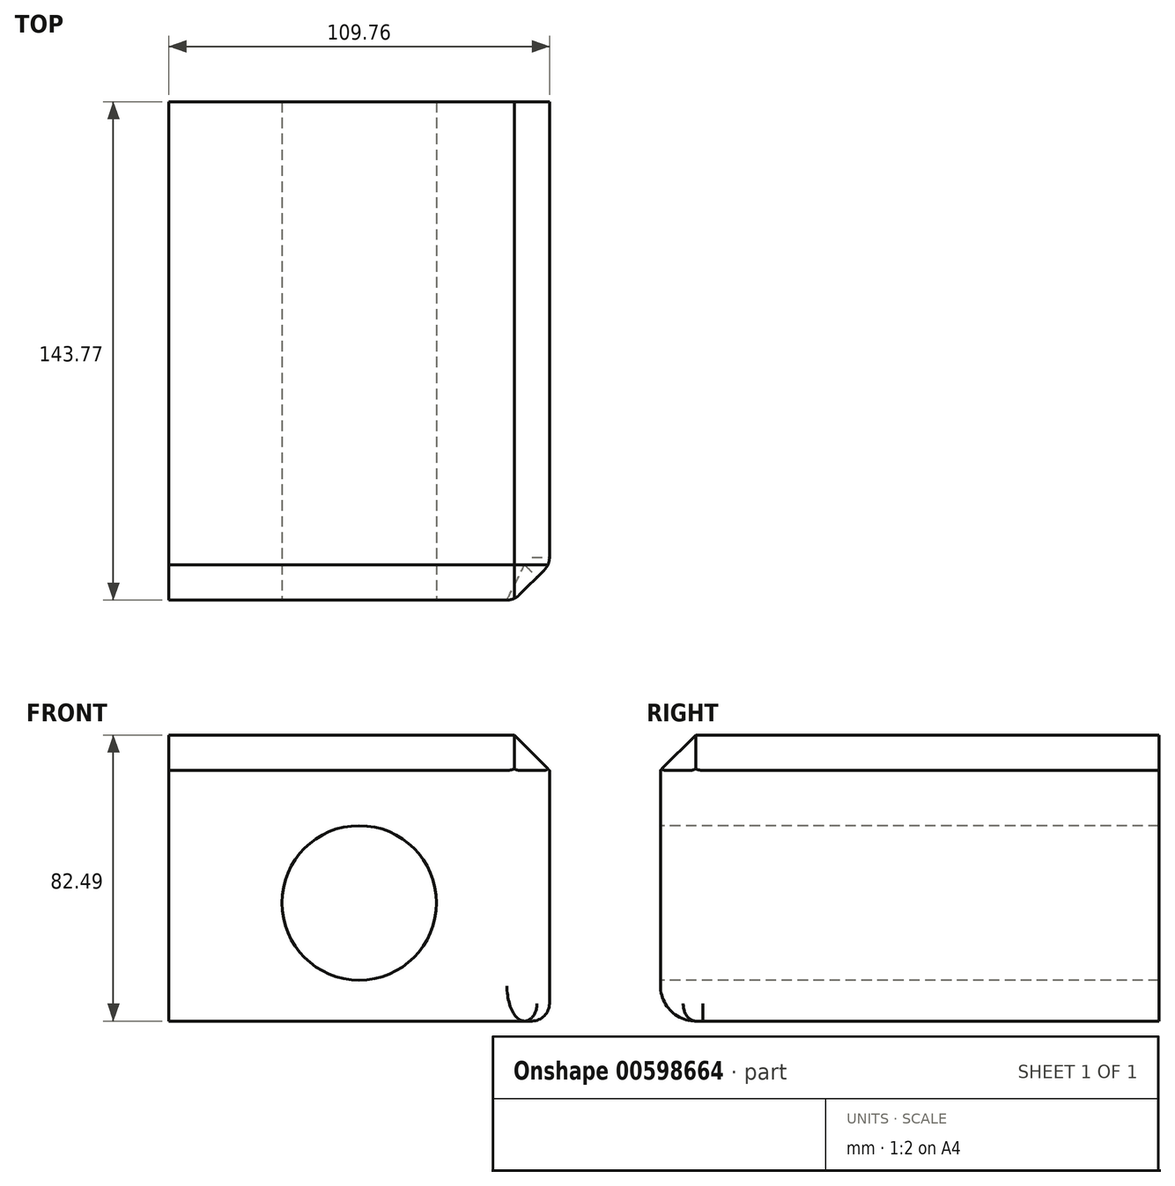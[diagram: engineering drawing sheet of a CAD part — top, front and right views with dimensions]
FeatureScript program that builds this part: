
annotation { "Feature Type Name" : "Feature", "Feature Type Description" : "" }
export const myFeature = defineFeature(function(context is Context, id is Id, definition is map)
    precondition{}
    {
        {
            var Q0;
            Q0=qCreatedBy(makeId("Front.planeOp"),FACE);
            var sketch = newSketch(context, id + "F0", { "sketchPlane" : qUnion([Q0])});
            skLineSegment(sketch, "E0.bottom", {"start": v(-39.35, 48.4) * mm, "end": v(70.41, 48.4) * mm});
            skLineSegment(sketch, "E0.top", {"start": v(-39.35, -34.1) * mm, "end": v(70.41, -34.1) * mm});
            skLineSegment(sketch, "E0.left", {"start": v(-39.35, 48.4) * mm, "end": v(-39.35, -34.1) * mm});
            skLineSegment(sketch, "E0.right", {"start": v(70.41, 48.4) * mm, "end": v(70.41, -34.1) * mm});
            skSolve(sketch);
        }
        {
            var Q0;
            Q0=makeQuery(id+"F0.imprint","IMPRINT",FACE,{"disambiguationData":[TD([[makeQuery(id+"F0.imprint","IMPRINT",EDGE,{"derivedFrom":sQuery(id+"F0.wireOp",EDGE,"E0.bottom")}),-1.0]])]});
            extrude(context, id + "F1", {"entities" : qUnion([Q0]), "depth" : 143.77 * mm, "offsetDistance" : 25.4 * mm});
        }
        {
            var Q0;
            Q0=makeQuery(id+"F1.opExtrude","CAP_FACE",FACE,{"disambiguationData":[OSD([sQuery(id+"F0.wireOp",EDGE,"E0.bottom"),sQuery(id+"F0.wireOp",EDGE,"E0.top"),sQuery(id+"F0.wireOp",EDGE,"E0.left"),sQuery(id+"F0.wireOp",EDGE,"E0.right")])],"isStart":false});
            var sketch = newSketch(context, id + "F2", { "sketchPlane" : qUnion([Q0])});
            skCircle(sketch, "E1", {"center": v(15.53, 0) * mm, "radius": 22.28 * mm});
            skPoint(sketch, "E1.centerSnap0", {"position": v(15.53, 48.4) * mm});
            skSolve(sketch);
        }
        {
            var Q0;
            Q0 = qSketchRegion(id + "F2", true);
            extrude(context, id + "F3", {"entities" : qUnion([Q0]), "operationType" : NewBodyOperationType.REMOVE, "oppositeDirection" : true, "depth" : 400.07 * mm, "offsetDistance" : 25.4 * mm});
        }
        {
            var Q0;
            Q0=makeQuery(id+"F1.opExtrude","SWEPT_EDGE",EDGE,{"disambiguationData":[OSD([sQuery(id+"F0.wireOp",EDGE,"E0.bottom"),sQuery(id+"F0.wireOp",EDGE,"E0.right")])]});
            var Q1;
            Q1=makeQuery(id+"F1.opExtrude","CAP_EDGE",EDGE,{"disambiguationData":[OSD([sQuery(id+"F0.wireOp",EDGE,"E0.bottom")])],"isStart":false});
            var Q2;
            Q2=makeQuery(id+"F1.opExtrude","CAP_EDGE",EDGE,{"disambiguationData":[OSD([sQuery(id+"F0.wireOp",EDGE,"E0.right")])],"isStart":false});
            chamfer(context, id + "F4", {"entities" : qUnion([Q0, Q1, Q2]), "width" : 10.16 * mm, "tangentPropagation" : true});
        }
        {
            var Q0;
            Q0=makeQuery(id+"F1.opExtrude","CAP_EDGE",EDGE,{"disambiguationData":[OSD([sQuery(id+"F0.wireOp",EDGE,"E0.top")])],"isStart":false});
            fillet(context, id + "F5", {"entities" : qUnion([Q0]), "radius" : 10.16 * mm, "tangentPropagation" : true, "allowEdgeOverflow" : false});
        }
        {
            var Q0;
            Q0=makeQuery(id+"F1.opExtrude","SWEPT_EDGE",EDGE,{"disambiguationData":[OSD([sQuery(id+"F0.wireOp",EDGE,"E0.top"),sQuery(id+"F0.wireOp",EDGE,"E0.right")])]});
            fillet(context, id + "F6", {"entities" : qUnion([Q0]), "radius" : 5.08 * mm, "tangentPropagation" : true, "allowEdgeOverflow" : false});
        }
        {
            var Q0;
            {var subQ0=sQuery(id+"F0.wireOp",EDGE,"E0.right");Q0=makeQuery(id+"F4.opChamfer","BLEND_EDGE",EDGE,{"blendedFrom":[makeQuery(id+"F1.opExtrude","CAP_EDGE",EDGE,{"disambiguationData":[OSD([subQ0])],"isStart":false}),makeQuery(id+"F1.opExtrude","SWEPT_FACE",FACE,{"disambiguationData":[OSD([subQ0])]})],"blendedInto":[makeQuery(id+"F1.opExtrude","SWEPT_FACE",FACE,{"disambiguationData":[OSD([subQ0])]})]});}
            var Q1;
            {var subQ0=sQuery(id+"F0.wireOp",EDGE,"E0.right");Q1=makeQuery(id+"F4.opChamfer","BLEND_EDGE",EDGE,{"blendedFrom":[makeQuery(id+"F1.opExtrude","CAP_EDGE",EDGE,{"disambiguationData":[OSD([subQ0])],"isStart":false}),makeQuery(id+"F1.opExtrude","CAP_FACE",FACE,{"disambiguationData":[OSD([sQuery(id+"F0.wireOp",EDGE,"E0.bottom"),sQuery(id+"F0.wireOp",EDGE,"E0.top"),sQuery(id+"F0.wireOp",EDGE,"E0.left"),subQ0])],"isStart":false})],"blendedInto":[makeQuery(id+"F1.opExtrude","CAP_FACE",FACE,{"disambiguationData":[OSD([sQuery(id+"F0.wireOp",EDGE,"E0.bottom"),sQuery(id+"F0.wireOp",EDGE,"E0.top"),sQuery(id+"F0.wireOp",EDGE,"E0.left"),subQ0])],"isStart":false})]});}
            fillet(context, id + "F7", {"entities" : qUnion([Q0, Q1]), "radius" : 5.08 * mm, "tangentPropagation" : true, "allowEdgeOverflow" : false});
        }
    });
